# Revit family: Casement_30.5_D_Side_Hung_Standard
name_source: partatom
category: Windows
revit_build: Autodesk Revit 2014 (Build: 20130308_1515(x64)
units: mm (PartAtom-declared; Revit-internal decimal feet)

## types (6) — shared parameters
Aluminium Thickness = 1 mm  [stored 0.00328084 ft]
Area Pane Top = 0.51 m²
Bead SG Gap = 13 mm  [stored 0.0426509 ft]
Casement Dimension = 31 mm  [stored 0.101706 ft]
Custom Sash Height = 1154 mm  [stored 3.78609 ft]
Custom Window Width = 590 mm  [stored 1.9357 ft]
DG Extrusion Start = 5 mm  [stored 0.0164042 ft]
DG Gasket Finish = Double Glazing Gasket Material
DG Thickness = 3 mm  [stored 0.00984252 ft]
DG Thickness Calc = 3 mm  [stored 0.00984252 ft]
Default Sill Height = 800 mm  [stored 2.62467 ft]
Depth Bead = 17 mm  [stored 0.0557743 ft]
Description = Window 30.5mm, Type D side hung
Double Glazing = No
Frame Center Offset = 15 mm  [stored 0.0492126 ft]
Height Panel 1 = 1140 mm
Height Sash = 1124 mm  [stored 3.68766 ft]
Height Sash Opening = 1154 mm  [stored 3.78609 ft]
Length Transom = 530 mm  [stored 1.73885 ft]
Limit Fixed Pane Height Max = 1800 mm  [stored 5.90551 ft]
Limit Fixed Pane Height Min = 200 mm  [stored 0.656168 ft]
Limit Sash Height Max = 1200 mm
Limit Sash Height Min = 300 mm  [stored 0.984252 ft]
Limit Sash Width Max = 600 mm  [stored 1.9685 ft]
Limit Sash Width Min = 300 mm  [stored 0.984252 ft]
Limit Window Height Max = 3030 mm  [stored 9.94094 ft]
Limit Window Height Min = 1430 mm  [stored 4.6916 ft]
Limit Window Width Max = 646 mm  [stored 2.11942 ft]
Limit Window Width Min = 346 mm
Manufacturer = Crealco
Max Pane Area = 0.51 m²
Max System DG One Piece Thickness = 3 mm  [stored 0.00984252 ft]
Max System DG Unit Thickness = 18 mm  [stored 0.0590551 ft]
Model = Casement 30.5
Offset Bead SG Center Reversed = 15 mm  [stored 0.0492126 ft]
Offset Panel 3 Bead Top = 1200 mm
Offset Sash Left = 23 mm  [stored 0.0754593 ft]
Offset Sash Top = 23 mm  [stored 0.0754593 ft]
Offset Transom Top = 1170 mm
Offset Window Exterior = 15 mm  [stored 0.0492126 ft]
SG Gasket Thickness = 6 mm  [stored 0.019685 ft]
Sash Center Offset = 12 mm  [stored 0.0393701 ft]
Sash Overlap = 7 mm  [stored 0.0229659 ft]
Sash Spacing Inner = 8 mm  [stored 0.0262467 ft]
Sash Width = 544 mm  [stored 1.78478 ft]
URL = http://www.crealco.co.za
Wall Closure = By host
Width = 590 mm  [stored 1.9357 ft]
Width Bead = 15 mm  [stored 0.0492126 ft]
Width Panel 1 = 530 mm  [stored 1.73885 ft]
Width Panel 3 = 530 mm  [stored 1.73885 ft]
Width Profile = 30 mm  [stored 0.0984252 ft]
Width Sash = 514 mm  [stored 1.68635 ft]
Width Sash Opening = 544 mm  [stored 1.78478 ft]
zero-valued in all types: Window Exterior Offset

## per-type parameters (varying)
| type | Area Pane Bottom | Clearvue SHGC Value | Clearvue U Value | Custom Windload | Custom Window Height | Energy Advantage SHGC Value | Energy Advantage U Value | Height | Height Panel 3 | Intruderprufe LowE SHGC Value | Intruderprufe LowE U Value | Intruderprufe SHGC Value | Intruderprufe U Value | Windload Design |
| 305-0615S-1000Pa | 0.13 m² | 0.572 | 6.12 | 1000 mm  [stored 3.28084 ft] | 1490 mm  [stored 4.88845 ft] | 0.513 | 4.77 | 1490 mm  [stored 4.88845 ft] | 260 mm  [stored 0.853018 ft] | 0.483 | 4.66 | 0.543 | 5.99 | 1000 mm  [stored 3.28084 ft] |
| 305-0618S-1000Pa | 0.29 m² | 0.595 | 6.1 | 1000 mm  [stored 3.28084 ft] | 1790 mm  [stored 5.8727 ft] | 0.533 | 4.68 | 1790 mm  [stored 5.8727 ft] | 560 mm  [stored 1.83727 ft] | 0.502 | 4.75 | 0.565 | 5.96 | 1000 mm  [stored 3.28084 ft] |
| 305-0615S-1500Pa | 0.13 m² | 0.572 | 6.12 | 1500 mm  [stored 4.92126 ft] | 1490 mm  [stored 4.88845 ft] | 0.513 | 4.77 | 1490 mm  [stored 4.88845 ft] | 260 mm  [stored 0.853018 ft] | 0.483 | 4.66 | 0.543 | 5.99 | 1500 mm  [stored 4.92126 ft] |
| 305-0615S-2000Pa | 0.13 m² | 0.572 | 6.12 | 2000 mm  [stored 6.56168 ft] | 1490 mm  [stored 4.88845 ft] | 0.513 | 4.77 | 1490 mm  [stored 4.88845 ft] | 260 mm  [stored 0.853018 ft] | 0.483 | 4.66 | 0.543 | 5.99 | 2000 mm  [stored 6.56168 ft] |
| 305-0618S-1500Pa | 0.29 m² | 0.595 | 6.1 | 1500 mm  [stored 4.92126 ft] | 1790 mm  [stored 5.8727 ft] | 0.533 | 4.68 | 1790 mm  [stored 5.8727 ft] | 560 mm  [stored 1.83727 ft] | 0.502 | 4.75 | 0.565 | 5.96 | 1500 mm  [stored 4.92126 ft] |
| 305-0618S-2000Pa | 0.29 m² | 0.595 | 6.1 | 2000 mm  [stored 6.56168 ft] | 1790 mm  [stored 5.8727 ft] | 0.533 | 4.68 | 1790 mm  [stored 5.8727 ft] | 560 mm  [stored 1.83727 ft] | 0.502 | 4.75 | 0.565 | 5.96 | 2000 mm  [stored 6.56168 ft] |

note: [stored X ft] marks values corroborated as IEEE doubles in the binary element streams (Revit-internal decimal feet)

## geometry (parser evidence)
native form markers: Blend x4, Extrusion x1, Sweep x25
no freeform markers — native parametric forms only
